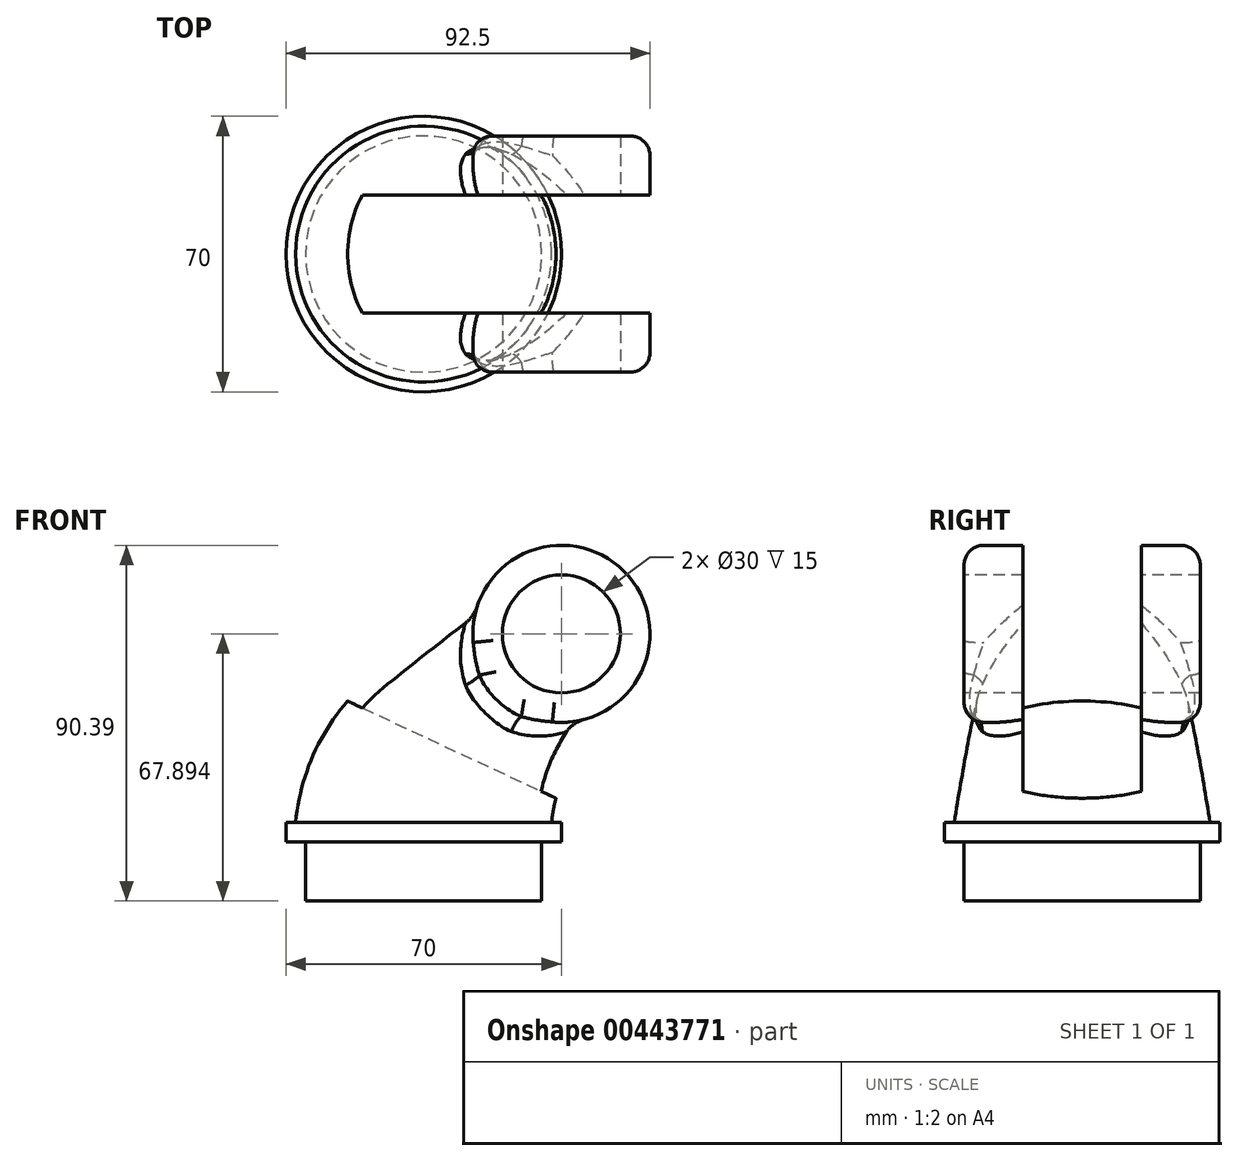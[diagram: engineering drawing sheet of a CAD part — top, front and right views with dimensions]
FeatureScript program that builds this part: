
annotation { "Feature Type Name" : "Feature", "Feature Type Description" : "" }
export const myFeature = defineFeature(function(context is Context, id is Id, definition is map)
    precondition{}
    {
        {
            var Q0;
            Q0=qCreatedBy(makeId("Top.planeOp"),FACE);
            var sketch = newSketch(context, id + "F0", { "sketchPlane" : qUnion([Q0])});
            skCircle(sketch, "E0", {"center": v(0, 0) * mm, "radius": 35 * mm});
            skSolve(sketch);
        }
        {
            var Q0;
            Q0 = qSketchRegion(id + "F0", true);
            extrude(context, id + "F1", {"entities" : qUnion([Q0]), "depth" : 5 * mm});
        }
        {
            var Q0;
            Q0=qCreatedBy(makeId("Front.planeOp"),FACE);
            var sketch = newSketch(context, id + "F2", { "sketchPlane" : qUnion([Q0])});
            skArc(sketch, "E1", {"start": v(17.6, 38.3) * mm, "mid": v(5.55, 23.37) * mm, "end": v(0, 5) * mm});
            skLineSegment(sketch, "E2", {"start": v(17.6, 38.3) * mm, "end": v(35, 52.9) * mm});
            skSolve(sketch);
        }
        {
            var Q0;
            Q0=sQuery(id+"F2.wireOp",EDGE,"E2");
            var Q1;
            Q1=sQuery(id+"F2.wireOp",VERTEX,"E2.end");
            cPlane(context, id + "F3", {"entities" : qUnion([Q0, Q1]), "cplaneType" : CPlaneType.LINE_POINT, "offset" : 25 * mm, "width" : 150 * mm, "height" : 150 * mm});
        }
        {
            var Q0;
            Q0=qCreatedBy(id+"F3.planeOp",FACE);
            var sketch = newSketch(context, id + "F4", { "sketchPlane" : qUnion([Q0])});
            skCircle(sketch, "E3", {"center": v(0, 18.02) * mm, "radius": 22.5 * mm});
            skSolve(sketch);
        }
        {
            var Q0;
            Q0=makeQuery(id+"F1.opExtrude","CAP_FACE",FACE,{"disambiguationData":[OSD([sQuery(id+"F0.wireOp",EDGE,"E0")])],"isStart":false});
            var sketch = newSketch(context, id + "F5", { "sketchPlane" : qUnion([Q0])});
            skCircle(sketch, "E4", {"center": v(0, 0) * mm, "radius": 32.5 * mm});
            skSolve(sketch);
        }
        {
            var Q0;
            Q0=qCreatedBy(makeId("Front.planeOp"),FACE);
            var sketch = newSketch(context, id + "F6", { "sketchPlane" : qUnion([Q0])});
            skArc(sketch, "E5", {"start": v(-13.25, 41.78) * mm, "mid": v(-26.5, 25.3) * mm, "end": v(-32.5, 5) * mm});
            skLineSegment(sketch, "E6", {"start": v(-13.25, 41.78) * mm, "end": v(20.54, 70.13) * mm});
            skSolve(sketch);
        }
        {
            var Q0;
            Q0=qCreatedBy(makeId("Front.planeOp"),FACE);
            var sketch = newSketch(context, id + "F7", { "sketchPlane" : qUnion([Q0])});
            skArc(sketch, "E7", {"start": v(48.46, 34.82) * mm, "mid": v(37.6, 21.45) * mm, "end": v(32.5, 5) * mm});
            skLineSegment(sketch, "E8", {"start": v(48.46, 34.82) * mm, "end": v(49.46, 35.66) * mm});
            skSolve(sketch);
        }
        {
            var Q1;
            Q1=makeQuery(id+"F5.imprint","IMPRINT",FACE,{"disambiguationData":[TD([[makeQuery(id+"F5.imprint","IMPRINT",EDGE,{"derivedFrom":sQuery(id+"F5.wireOp",EDGE,"E4")}),1.0]])]});
            var Q2;
            Q2=makeQuery(id+"F4.imprint","IMPRINT",FACE,{"disambiguationData":[TD([[makeQuery(id+"F4.imprint","IMPRINT",EDGE,{"derivedFrom":sQuery(id+"F4.wireOp",EDGE,"E3")}),1.0]])]});
            var Q3;
            Q3 = qConstructionFilter(qBodyType(qCreatedBy(id + "F7" ,EDGE), BodyType.WIRE), ConstructionObject.NO);
            var Q4;
            Q4 = qConstructionFilter(qBodyType(qCreatedBy(id + "F6" ,EDGE), BodyType.WIRE), ConstructionObject.NO);
            loft(context, id + "F8", {"operationType" : NewBodyOperationType.ADD, "addGuides" : true, "sheetProfilesArray" : [{ "sheetProfileEntities" : qUnion([Q1]) }, { "sheetProfileEntities" : qUnion([Q2]) }], "guidesArray" : [{ "guideEntities" : qUnion([Q3]), "guideDerivativeType" : LoftGuideDerivativeType.DEFAULT, "guideDerivativeMagnitude" : 1 }, { "guideEntities" : qUnion([Q4]), "guideDerivativeType" : LoftGuideDerivativeType.DEFAULT, "guideDerivativeMagnitude" : 1 }]});
        }
        {
            var Q0;
            Q0=qCreatedBy(makeId("Front.planeOp"),FACE);
            var sketch = newSketch(context, id + "F9", { "sketchPlane" : qUnion([Q0])});
            skCircle(sketch, "E9", {"center": v(35, 52.9) * mm, "radius": 22.5 * mm});
            skSolve(sketch);
        }
        {
            var Q0;
            Q0 = qSketchRegion(id + "F9", true);
            extrude(context, id + "F10", {"entities" : qUnion([Q0]), "operationType" : NewBodyOperationType.ADD, "endBound" : BoundingType.SYMMETRIC, "depth" : 60 * mm});
        }
        {
            var Q0;
            Q0=makeQuery(id+"F10.boolean.opBoolean","INTERSECT",EDGE,{"disambiguationData":[OD(0.0)],"derivedFrom":[makeQuery(id+"F8.opLoft","SWEPT_FACE",FACE,{"disambiguationData":[OSD([sQuery(id+"F4.wireOp",EDGE,"E3"),sQuery(id+"F5.wireOp",EDGE,"E4"),sQuery(id+"F6.wireOp",VERTEX,"E6.start"),sQuery(id+"F6.wireOp",EDGE,"E5"),sQuery(id+"F6.wireOp",EDGE,"E6"),sQuery(id+"F7.wireOp",VERTEX,"E8.start"),sQuery(id+"F7.wireOp",EDGE,"E7"),sQuery(id+"F7.wireOp",EDGE,"E8")])]}),makeQuery(id+"F10.opExtrude","SWEPT_FACE",FACE,{"disambiguationData":[OSD([sQuery(id+"F9.wireOp",EDGE,"E9")])]})]});
            var Q1;
            Q1=makeQuery(id+"F10.boolean.opBoolean","INTERSECT",EDGE,{"disambiguationData":[OD(1.0)],"derivedFrom":[makeQuery(id+"F8.opLoft","SWEPT_FACE",FACE,{"disambiguationData":[OSD([sQuery(id+"F4.wireOp",EDGE,"E3"),sQuery(id+"F5.wireOp",EDGE,"E4"),sQuery(id+"F6.wireOp",VERTEX,"E6.start"),sQuery(id+"F6.wireOp",EDGE,"E5"),sQuery(id+"F6.wireOp",EDGE,"E6"),sQuery(id+"F7.wireOp",VERTEX,"E8.start"),sQuery(id+"F7.wireOp",EDGE,"E7"),sQuery(id+"F7.wireOp",EDGE,"E8")])]}),makeQuery(id+"F10.opExtrude","SWEPT_FACE",FACE,{"disambiguationData":[OSD([sQuery(id+"F9.wireOp",EDGE,"E9")])]})]});
            fillet(context, id + "F11", {"entities" : qUnion([Q0, Q1]), "radius" : 5 * mm, "tangentPropagation" : true, "allowEdgeOverflow" : false});
        }
        {
            var Q0;
            Q0=makeQuery(id+"F10.opExtrude","CAP_EDGE",EDGE,{"disambiguationData":[OSD([sQuery(id+"F9.wireOp",EDGE,"E9")])],"isStart":false});
            var Q1;
            Q1=makeQuery(id+"F10.opExtrude","CAP_EDGE",EDGE,{"disambiguationData":[OSD([sQuery(id+"F9.wireOp",EDGE,"E9")])],"isStart":true});
            fillet(context, id + "F12", {"entities" : qUnion([Q0, Q1]), "radius" : 5 * mm, "tangentPropagation" : true, "allowEdgeOverflow" : false});
        }
        {
            var Q0;
            Q0=makeQuery(id+"F10.opExtrude","CAP_FACE",FACE,{"disambiguationData":[OSD([sQuery(id+"F9.wireOp",EDGE,"E9")])],"isStart":false});
            var sketch = newSketch(context, id + "F13", { "sketchPlane" : qUnion([Q0])});
            skCircle(sketch, "E10", {"center": v(35, 52.9) * mm, "radius": 15 * mm});
            skSolve(sketch);
        }
        {
            var Q0;
            Q0 = qSketchRegion(id + "F13", true);
            extrude(context, id + "F14", {"entities" : qUnion([Q0]), "operationType" : NewBodyOperationType.REMOVE, "endBound" : BoundingType.THROUGH_ALL, "oppositeDirection" : true, "depth" : 25 * mm});
        }
        {
            var Q0;
            Q0=qCreatedBy(makeId("Front.planeOp"),FACE);
            var sketch = newSketch(context, id + "F15", { "sketchPlane" : qUnion([Q0])});
            skLineSegment(sketch, "E11", {"start": v(-104.18, 75.4) * mm, "end": v(57.5, 0) * mm});
            skLineSegment(sketch, "E12", {"start": v(57.5, 75.4) * mm, "end": v(57.5, 0) * mm});
            skLineSegment(sketch, "E13", {"start": v(-104.18, 75.4) * mm, "end": v(57.5, 75.4) * mm});
            skSolve(sketch);
        }
        {
            var Q0;
            Q0 = qSketchRegion(id + "F15", true);
            extrude(context, id + "F16", {"entities" : qUnion([Q0]), "operationType" : NewBodyOperationType.REMOVE, "endBound" : BoundingType.SYMMETRIC, "oppositeDirection" : true, "depth" : 30 * mm});
        }
        {
            var Q0;
            Q0=qCreatedBy(makeId("Front.planeOp"),FACE);
            var sketch = newSketch(context, id + "F17", { "sketchPlane" : qUnion([Q0])});
            skLineSegment(sketch, "E14.bottom", {"start": v(0, 0) * mm, "end": v(-30, 0) * mm});
            skLineSegment(sketch, "E14.top", {"start": v(0, -15) * mm, "end": v(-30, -15) * mm});
            skLineSegment(sketch, "E14.left", {"start": v(0, 0) * mm, "end": v(0, -15) * mm});
            skLineSegment(sketch, "E14.right", {"start": v(-30, 0) * mm, "end": v(-30, -15) * mm});
            skSolve(sketch);
        }
        {
            var Q0;
            Q0=makeQuery(id+"F17.imprint","IMPRINT",FACE,{"disambiguationData":[TD([[makeQuery(id+"F17.imprint","IMPRINT",EDGE,{"derivedFrom":sQuery(id+"F17.wireOp",EDGE,"E14.bottom")}),1.0]])]});
            var Q1;
            Q1=sQuery(id+"F17.wireOp",EDGE,"E14.left");
            revolve(context, id + "F18", {"operationType" : NewBodyOperationType.ADD, "entities" : qUnion([Q0]), "axis" : qUnion([Q1]), "revolveType" : RevolveType.FULL});
        }
    });
